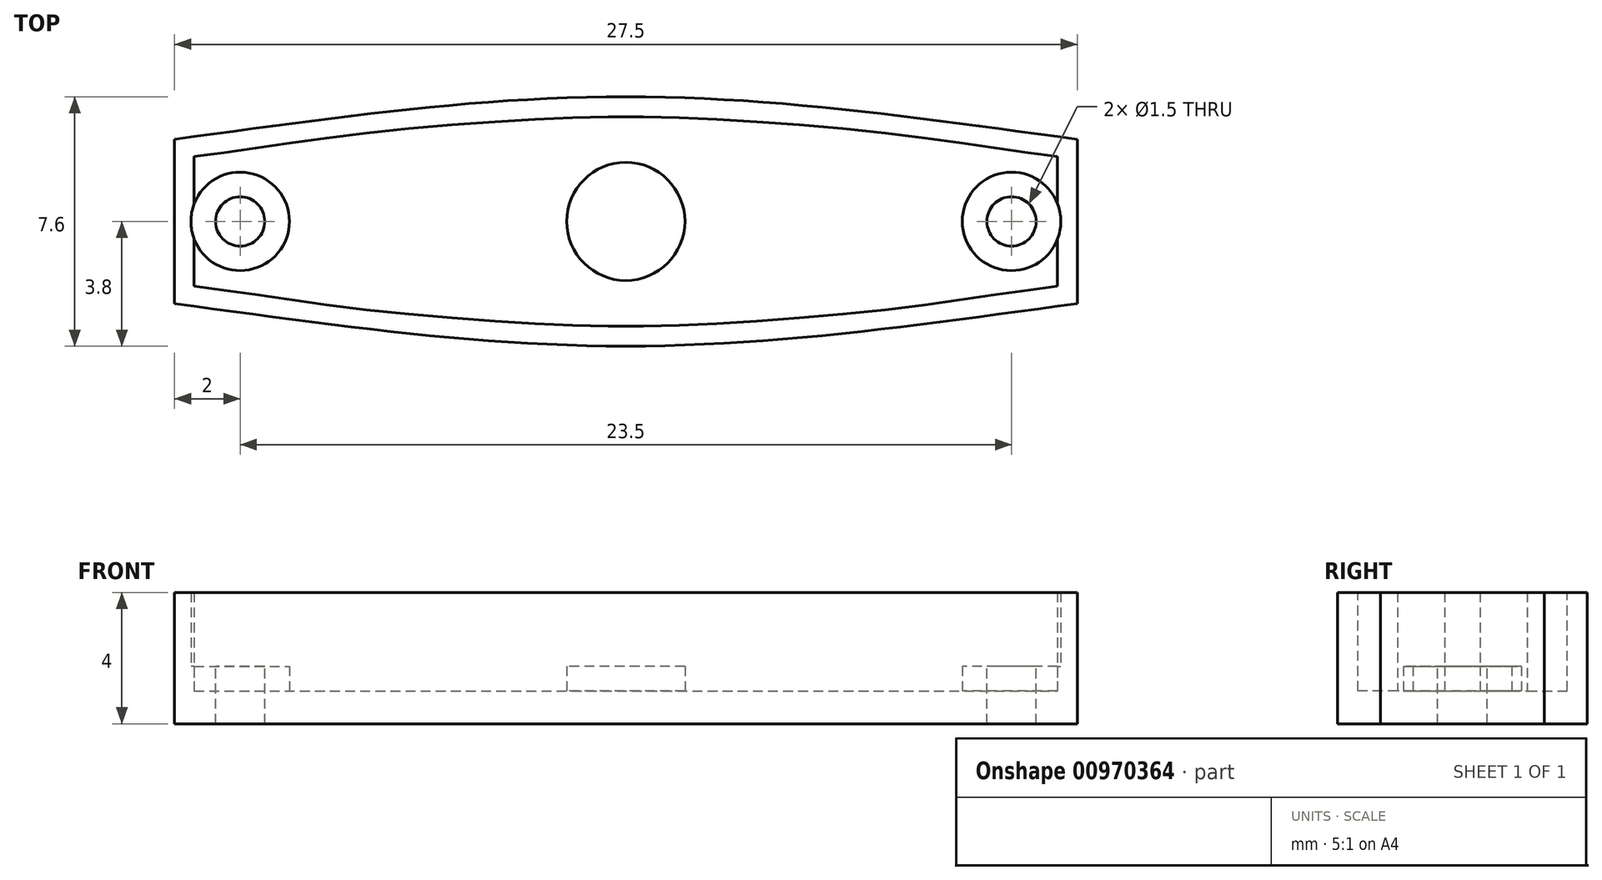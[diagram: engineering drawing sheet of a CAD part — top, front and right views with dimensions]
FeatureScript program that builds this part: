
annotation { "Feature Type Name" : "Feature", "Feature Type Description" : "" }
export const myFeature = defineFeature(function(context is Context, id is Id, definition is map)
    precondition{}
    {
        {
            var Q0;
            Q0=qCreatedBy(makeId("Top.planeOp"),FACE);
            var sketch = newSketch(context, id + "F0", { "sketchPlane" : qUnion([Q0])});
            skLineSegment(sketch, "E0.bottom", {"start": v(13.75, 3.8) * mm, "end": v(-13.75, 3.8) * mm});
            skLineSegment(sketch, "E0.top", {"start": v(13.75, -3.8) * mm, "end": v(-13.75, -3.8) * mm});
            skLineSegment(sketch, "E0.left", {"start": v(13.75, 3.8) * mm, "end": v(13.75, -3.8) * mm});
            skLineSegment(sketch, "E0.right", {"start": v(-13.75, 3.8) * mm, "end": v(-13.75, -3.8) * mm});
            skPoint(sketch, "E0.middle", {"position": v(0, 0) * mm});
            skLineSegment(sketch, "E1.bottom", {"start": v(13.75, 2.5) * mm, "end": v(-13.75, 2.5) * mm});
            skLineSegment(sketch, "E1.top", {"start": v(13.75, -2.5) * mm, "end": v(-13.75, -2.5) * mm});
            skLineSegment(sketch, "E1.left", {"start": v(13.75, 2.5) * mm, "end": v(13.75, -2.5) * mm});
            skLineSegment(sketch, "E1.right", {"start": v(-13.75, 2.5) * mm, "end": v(-13.75, -2.5) * mm});
            skFitSpline(sketch, "E2", {"points": [v(-13.75, 2.5) * mm, v(0, 3.8) * mm, v(13.75, 2.5) * mm], "startDerivative": vector(27.5, 3.75) * mm, "endDerivative": vector(27.5, -3.75) * mm});
            skFitSpline(sketch, "E3", {"points": [v(-13.75, -2.5) * mm, v(0, -3.8) * mm, v(13.75, -2.5) * mm], "startDerivative": vector(27.5, -3.75) * mm, "endDerivative": vector(27.5, 3.75) * mm});
            skSolve(sketch);
        }
        {
            var Q0;
            {var subQ0=sQuery(id+"F0.wireOp",EDGE,"E1.bottom");Q0=makeQuery(id+"F0.imprint","IMPRINT",FACE,{"disambiguationData":[TD([[makeQuery(id+"F0.imprint","IMPRINT",EDGE,{"derivedFrom":subQ0}),-1.0]])]});}
            var Q1;
            Q1=makeQuery(id+"F0.imprint","IMPRINT",FACE,{"disambiguationData":[TD([[makeQuery(id+"F0.imprint","IMPRINT",EDGE,{"derivedFrom":sQuery(id+"F0.wireOp",EDGE,"E1.bottom")}),1.0]])]});
            var Q2;
            {var subQ0=sQuery(id+"F0.wireOp",EDGE,"E1.top");Q2=makeQuery(id+"F0.imprint","IMPRINT",FACE,{"disambiguationData":[TD([[makeQuery(id+"F0.imprint","IMPRINT",EDGE,{"derivedFrom":subQ0}),1.0]])]});}
            extrude(context, id + "F1", {"entities" : qUnion([Q0, Q1, Q2]), "depth" : 1 * mm, "offsetDistance" : 25.4 * mm});
        }
        {
            var Q0;
            Q0=makeQuery(id+"F1.opExtrude","CAP_FACE",FACE,{"disambiguationData":[OSD([sQuery(id+"F0.wireOp",EDGE,"E1.left"),sQuery(id+"F0.wireOp",EDGE,"E1.right"),sQuery(id+"F0.wireOp",EDGE,"E2"),sQuery(id+"F0.wireOp",EDGE,"E3")])],"isStart":false});
            var sketch = newSketch(context, id + "F2", { "sketchPlane" : qUnion([Q0])});
            skCircle(sketch, "E4", {"center": v(-11.75, 0) * mm, "radius": 1.5 * mm});
            skCircle(sketch, "E5", {"center": v(11.75, 0) * mm, "radius": 1.5 * mm});
            skCircle(sketch, "E6", {"center": v(0, 0) * mm, "radius": 1.8 * mm});
            skSolve(sketch);
        }
        {
            var Q0;
            Q0 = qSketchRegion(id + "F2", true);
            extrude(context, id + "F3", {"entities" : qUnion([Q0]), "operationType" : NewBodyOperationType.ADD, "depth" : .75 * mm, "offsetDistance" : 25.4 * mm});
        }
        {
            var Q0;
            Q0=makeQuery(id+"F3.opExtrude","CAP_FACE",FACE,{"disambiguationData":[OSD([sQuery(id+"F2.wireOp",EDGE,"E5")])],"isStart":false});
            var sketch = newSketch(context, id + "F4", { "sketchPlane" : qUnion([Q0])});
            skCircle(sketch, "E7", {"center": v(-11.75, 0) * mm, "radius": 0.75 * mm});
            skCircle(sketch, "E8", {"center": v(11.75, 0) * mm, "radius": 0.75 * mm});
            skSolve(sketch);
        }
        {
            var Q0;
            Q0 = qSketchRegion(id + "F4", true);
            extrude(context, id + "F5", {"entities" : qUnion([Q0]), "operationType" : NewBodyOperationType.REMOVE, "oppositeDirection" : true, "depth" : 25.4 * mm, "offsetDistance" : 25.4 * mm});
        }
        {
            var Q0;
            Q0=makeQuery(id+"F1.opExtrude","CAP_FACE",FACE,{"disambiguationData":[OSD([sQuery(id+"F0.wireOp",EDGE,"E1.left"),sQuery(id+"F0.wireOp",EDGE,"E1.right"),sQuery(id+"F0.wireOp",EDGE,"E2"),sQuery(id+"F0.wireOp",EDGE,"E3")])],"isStart":false});
            var sketch = newSketch(context, id + "F6", { "sketchPlane" : qUnion([Q0])});
            skFitSpline(sketch, "E9.0", {"points": [v(13.67, 1.9) * mm, v(11.38, 2.22) * mm, v(7.95, 2.69) * mm, v(3.4, 3.07) * mm, v(0, 3.19) * mm, v(-3.4, 3.07) * mm, v(-7.95, 2.69) * mm, v(-11.38, 2.22) * mm, v(-13.67, 1.9) * mm]});
            skLineSegment(sketch, "E9.1", {"start": v(13.15, -1.98) * mm, "end": v(13.15, 1.98) * mm});
            skFitSpline(sketch, "E9.2", {"points": [v(-13.67, -1.9) * mm, v(-11.38, -2.22) * mm, v(-7.95, -2.69) * mm, v(-3.4, -3.07) * mm, v(0, -3.19) * mm, v(3.4, -3.07) * mm, v(7.95, -2.69) * mm, v(11.38, -2.22) * mm, v(13.67, -1.9) * mm]});
            skLineSegment(sketch, "E9.3", {"start": v(-13.15, 1.98) * mm, "end": v(-13.15, -1.98) * mm});
            skSolve(sketch);
        }
        {
            var Q0;
            Q0=makeQuery(id+"F6.imprint","IMPRINT",FACE,{"disambiguationData":[TD([[makeQuery(id+"F6.imprint","IMPRINT",EDGE,{"derivedFrom":sQuery(id+"F6.wireOp",EDGE,"E9.0")}),-1.0]])]});
            extrude(context, id + "F7", {"entities" : qUnion([Q0]), "operationType" : NewBodyOperationType.ADD, "depth" : 3 * mm, "offsetDistance" : 25.4 * mm});
        }
    });
